# Revit family: Tub_Filler-Deck_Mounted-American_Standard-Flash-R9X0
name_source: partatom
category: Plumbing Fixtures
revit_build: Autodesk Revit 2014 (Build: 20130308_1515(x64)
units: mm (PartAtom-declared; Revit-internal decimal feet)

## types (2) — shared parameters
Assembly Code = D2020
COFaucet To Shower = 12"
CW Connection = Yes
CWFU = 3
Cold Water Connection Diameter = 1/2"
Cold Water Connection Radius = 1/4"
Default Elevation = 0"
HW Connection = Yes
HWFU = 3
Height = 7 1/8"
Hot Water Connection Diameter = 1"
Hot Water Connection Radius = 1/4"
Installation Type = Deck-Mounted
Length = 10"
Manufacturer = American Standard
Material = Metal-American Standard-099-Polished Brass
Price = Prices may vary. Please consult Manufacturer Representative for most up-to-date price list.
Product Documentation Link = https://www.americanstandard-us.com
Product URL = https://www.americanstandard-us.com
URL = http://www.americanstandard-us.com
Vent Connection = No
Waste Connection = No
Width = 1 3/8"
zero-valued in all types: WFU

## per-type parameters (varying)
| type | Description | Shower |
| R900 | R900 Flash Roman Tub Filler Rough Body – LESS Personal Shower | No |
| R910 | R910 Flash Roman Tub Filler Rough Body – WITH Personal Shower | Yes |

note: column(s) folded — value = type name in every type: Model

## geometry (parser evidence)
native form markers: Sweep x1
no freeform markers — native parametric forms only
